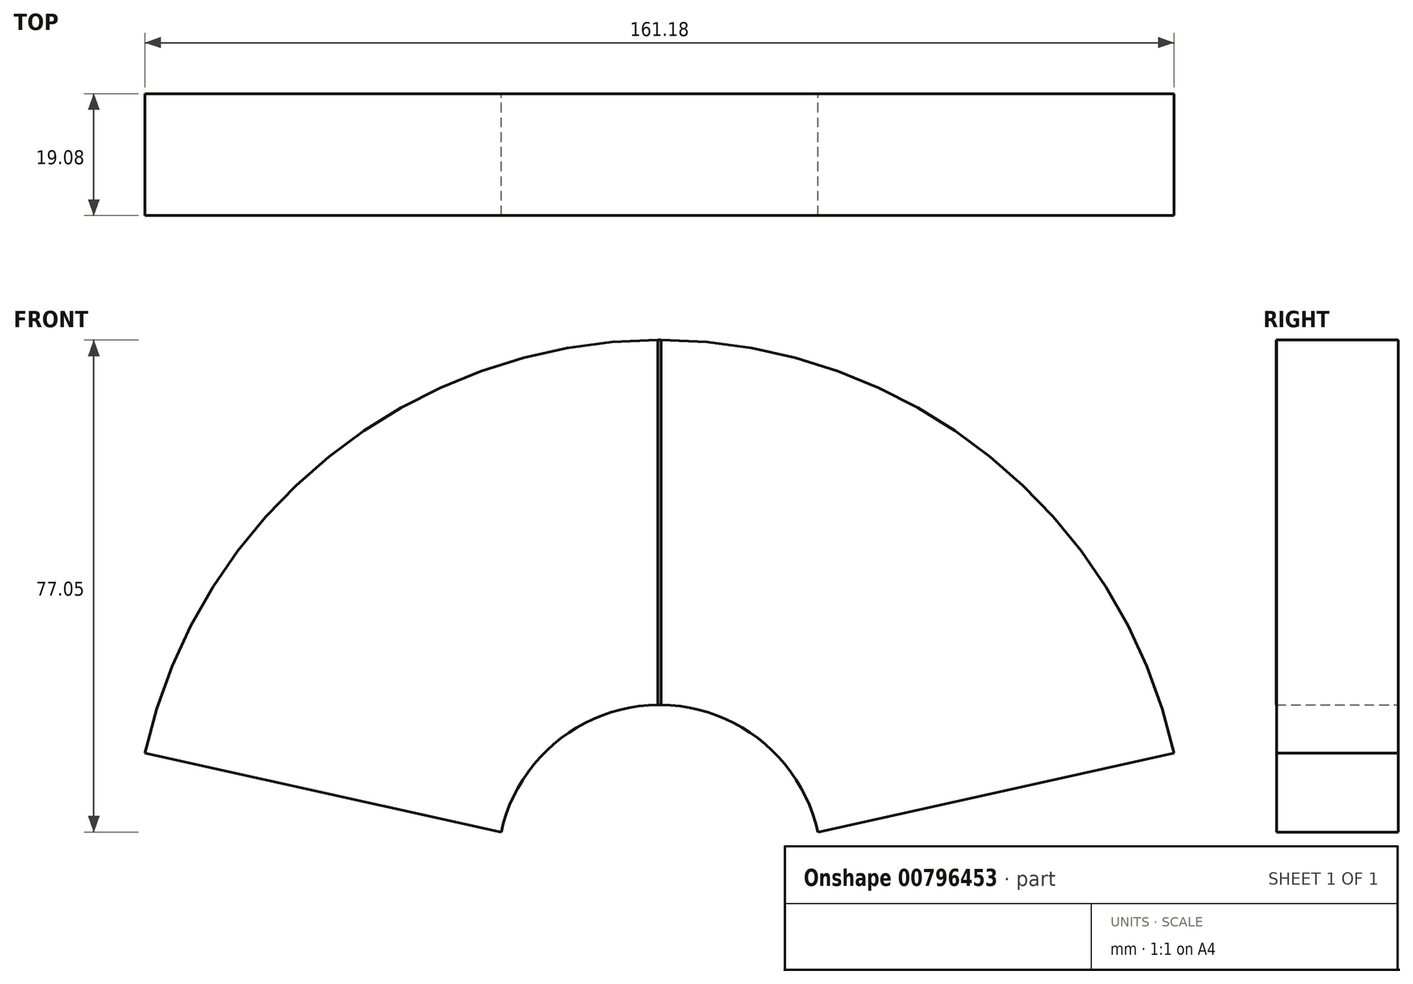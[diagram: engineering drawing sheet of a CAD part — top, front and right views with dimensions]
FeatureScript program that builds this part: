
annotation { "Feature Type Name" : "Feature", "Feature Type Description" : "" }
export const myFeature = defineFeature(function(context is Context, id is Id, definition is map)
    precondition{}
    {
        {
            var Q0;
            Q0=qCreatedBy(makeId("Front.planeOp"),FACE);
            var sketch = newSketch(context, id + "F0", { "sketchPlane" : qUnion([Q0])});
            skArc(sketch, "E0", {"start": v(24.8, 5.5) * mm, "mid": v(0, 25.4) * mm, "end": v(-24.8, 5.5) * mm});
            skArc(sketch, "E1", {"start": v(80.6, 17.87) * mm, "mid": v(0, 82.55) * mm, "end": v(-80.6, 17.87) * mm});
            skLineSegment(sketch, "E2", {"start": v(24.8, 5.5) * mm, "end": v(80.6, 17.87) * mm});
            skLineSegment(sketch, "E3", {"start": v(-24.8, 5.5) * mm, "end": v(-80.6, 17.87) * mm});
            skLineSegment(sketch, "E4", {"start": v(80.6, 17.87) * mm, "end": v(80.6, 0) * mm, "construction": true});
            skLineSegment(sketch, "E5", {"start": v(-80.6, 17.87) * mm, "end": v(-80.6, 0) * mm, "construction": true});
            skSolve(sketch);
        }
        {
            var Q0;
            Q0=makeQuery(id+"F0.imprint","IMPRINT",FACE,{"disambiguationData":[TD([[makeQuery(id+"F0.imprint","IMPRINT",EDGE,{"derivedFrom":sQuery(id+"F0.wireOp",EDGE,"E0")}),-1.0]])]});
            extrude(context, id + "F1", {"entities" : qUnion([Q0]), "depth" : 19.05 * mm, "offsetDistance" : 25.4 * mm});
        }
        {
            var Q0;
            Q0=makeQuery(id+"F1.opExtrude","CAP_FACE",FACE,{"disambiguationData":[OSD([sQuery(id+"F0.wireOp",EDGE,"E0"),sQuery(id+"F0.wireOp",EDGE,"E1"),sQuery(id+"F0.wireOp",EDGE,"E2"),sQuery(id+"F0.wireOp",EDGE,"E3")])],"isStart":false});
            var sketch = newSketch(context, id + "F2", { "sketchPlane" : qUnion([Q0])});
            skLineSegment(sketch, "E6", {"start": v(0, 25.4) * mm, "end": v(0.25, 25.4) * mm});
            skLineSegment(sketch, "E7", {"start": v(0.25, 25.4) * mm, "end": v(0.25, 82.55) * mm});
            skLineSegment(sketch, "E8", {"start": v(0.25, 82.55) * mm, "end": v(0, 82.55) * mm});
            skLineSegment(sketch, "E9", {"start": v(0, 82.55) * mm, "end": v(-0.25, 82.55) * mm});
            skLineSegment(sketch, "E10", {"start": v(-0.25, 82.55) * mm, "end": v(-0.25, 25.4) * mm});
            skLineSegment(sketch, "E11", {"start": v(-0.25, 25.4) * mm, "end": v(0, 25.4) * mm});
            skSolve(sketch);
        }
        {
            var Q0;
            {var subQ5=sQuery(id+"F2.wireOp",EDGE,"E6");Q0=makeQuery(id+"F2.imprint","IMPRINT",FACE,{"disambiguationData":[TD([[makeQuery(id+"F2.imprint","IMPRINT",EDGE,{"derivedFrom":subQ5}),1.0]])]});}
            extrude(context, id + "F3", {"entities" : qUnion([Q0]), "operationType" : NewBodyOperationType.ADD, "depth" : 0.03 * mm, "offsetDistance" : 25.4 * mm});
        }
    });
